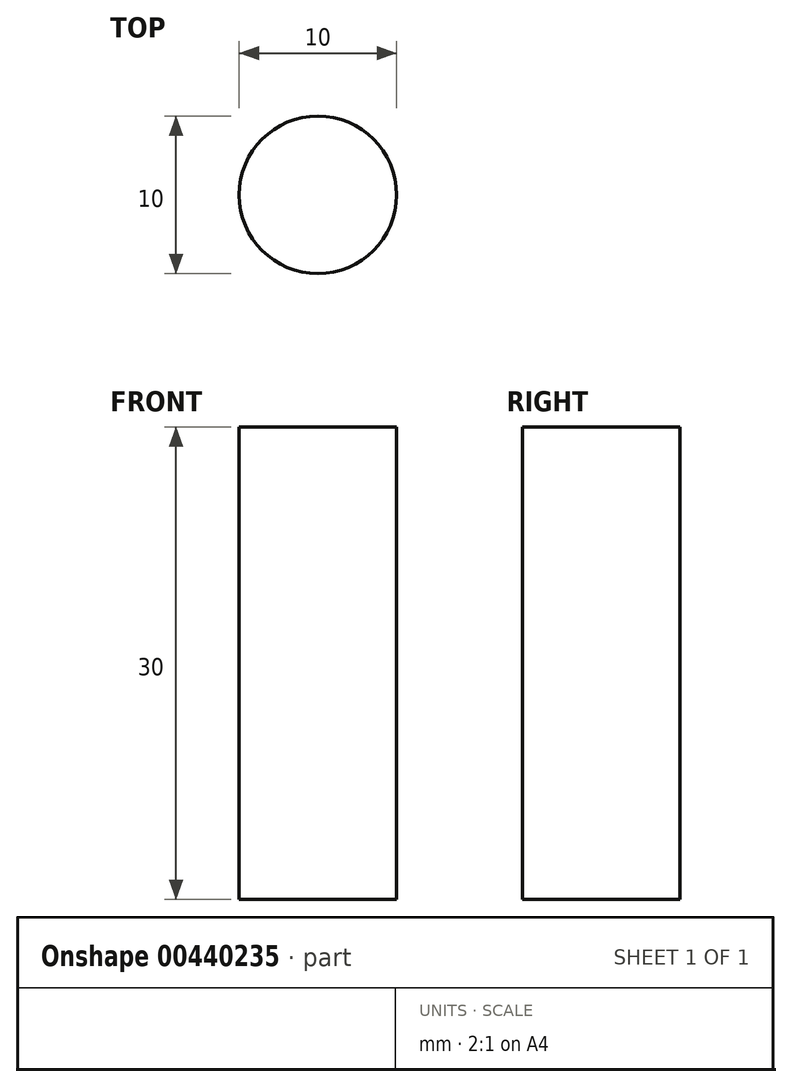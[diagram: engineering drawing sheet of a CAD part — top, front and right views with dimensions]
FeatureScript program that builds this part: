
annotation { "Feature Type Name" : "Feature", "Feature Type Description" : "" }
export const myFeature = defineFeature(function(context is Context, id is Id, definition is map)
    precondition{}
    {
        {
            var Q0;
            Q0=qCreatedBy(makeId("Top.planeOp"),FACE);
            var sketch = newSketch(context, id + "F0", { "sketchPlane" : qUnion([Q0])});
            skCircle(sketch, "E0", {"center": v(0, 0) * mm, "radius": 5 * mm});
            skSolve(sketch);
        }
        {
            var Q0;
            Q0 = qSketchRegion(id + "F0", true);
            extrude(context, id + "F1", {"entities" : qUnion([Q0]), "depth" : 30 * mm});
        }
    });
